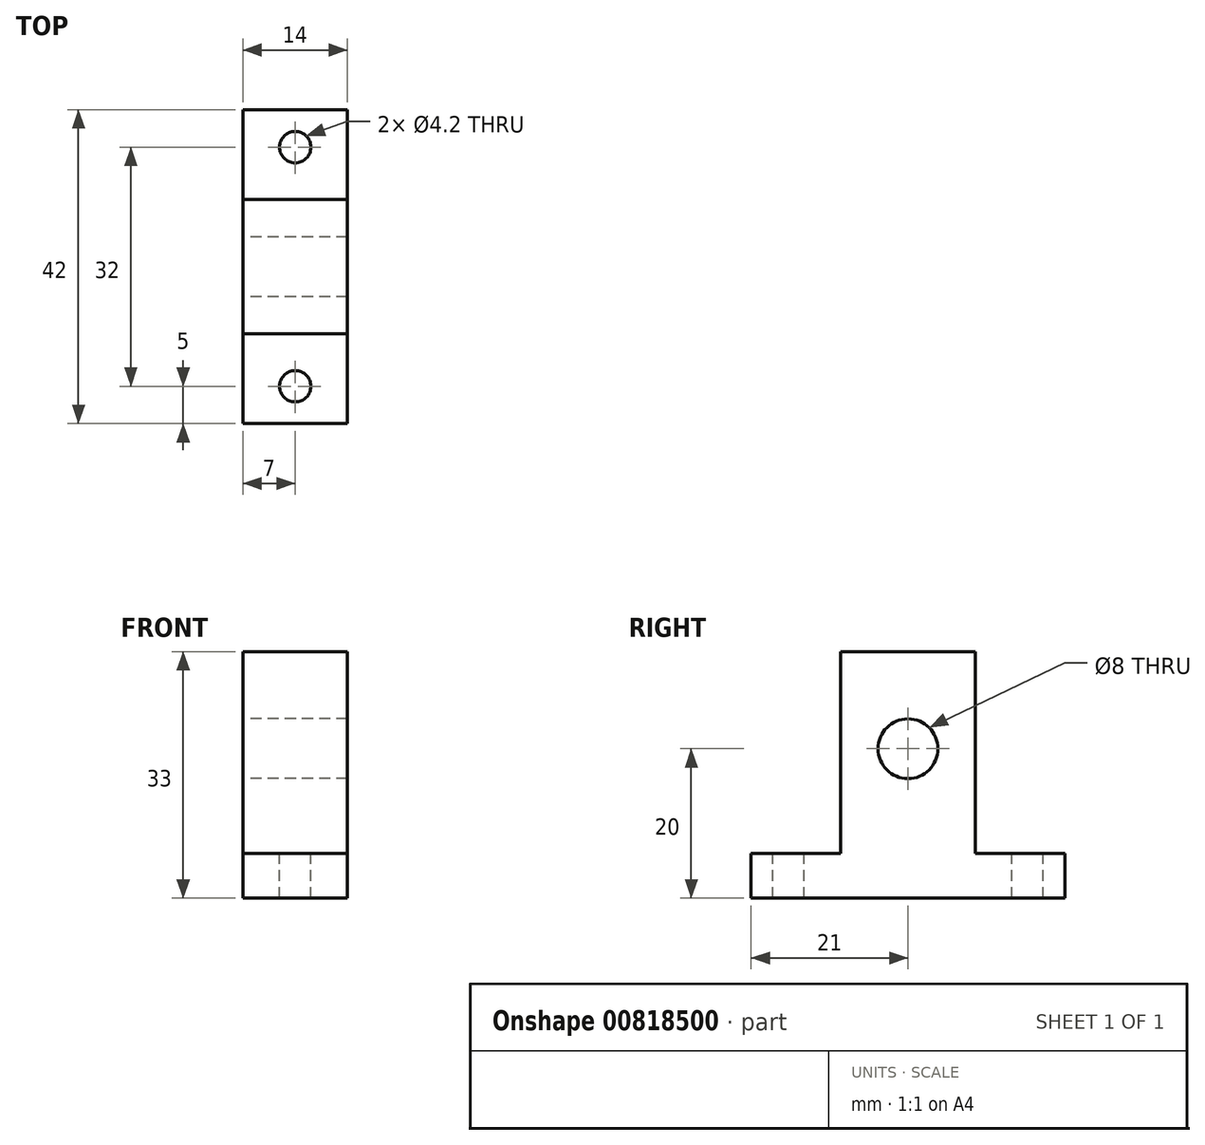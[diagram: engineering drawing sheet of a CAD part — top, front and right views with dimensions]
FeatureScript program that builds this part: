
annotation { "Feature Type Name" : "Feature", "Feature Type Description" : "" }
export const myFeature = defineFeature(function(context is Context, id is Id, definition is map)
    precondition{}
    {
        {
            var Q0;
            Q0=qCreatedBy(makeId("Right.planeOp"),FACE);
            var sketch = newSketch(context, id + "F0", { "sketchPlane" : qUnion([Q0])});
            skCircle(sketch, "E0", {"center": v(0, 20) * mm, "radius": 4 * mm});
            skLineSegment(sketch, "E1", {"start": v(0, 0) * mm, "end": v(-21, 0) * mm});
            skLineSegment(sketch, "E2", {"start": v(-21, 0) * mm, "end": v(-21, 6) * mm});
            skLineSegment(sketch, "E3", {"start": v(-21, 6) * mm, "end": v(-9, 6) * mm});
            skLineSegment(sketch, "E4", {"start": v(-9, 6) * mm, "end": v(-9, 33) * mm});
            skLineSegment(sketch, "E5", {"start": v(-9, 33) * mm, "end": v(0, 33) * mm});
            skLineSegment(sketch, "E6.MirrorCS", {"start": v(0, 0) * mm, "end": v(21, 0) * mm});
            skLineSegment(sketch, "E7.MirrorCS", {"start": v(21, 0) * mm, "end": v(21, 6) * mm});
            skLineSegment(sketch, "E8.MirrorCS", {"start": v(21, 6) * mm, "end": v(9, 6) * mm});
            skLineSegment(sketch, "E9.MirrorCS", {"start": v(9, 33) * mm, "end": v(0, 33) * mm});
            skLineSegment(sketch, "E10.MirrorCS", {"start": v(9, 6) * mm, "end": v(9, 33) * mm});
            skSolve(sketch);
        }
        {
            var Q0;
            Q0=makeQuery(id+"F0.imprint","IMPRINT",FACE,{"disambiguationData":[TD([[makeQuery(id+"F0.imprint","IMPRINT",EDGE,{"derivedFrom":sQuery(id+"F0.wireOp",EDGE,"E0")}),-1.0]])]});
            extrude(context, id + "F1", {"entities" : qUnion([Q0]), "endBound" : BoundingType.SYMMETRIC, "depth" : 14 * mm});
        }
        {
            var Q0;
            Q0=makeQuery(id+"F1.opExtrude","SWEPT_FACE",FACE,{"disambiguationData":[OSD([sQuery(id+"F0.wireOp",EDGE,"E3")])]});
            var sketch = newSketch(context, id + "F2", { "sketchPlane" : qUnion([Q0])});
            skSolve(sketch);
        }
        {
            var Q0;
            {var subQ0=sQuery(id+"F0.wireOp",EDGE,"E3");Q0=makeQuery(id+"F2.imprint","IMPRINT",FACE,{"disambiguationData":[TD([[makeQuery(id+"F2.imprint","IMPRINT",EDGE,{"derivedFrom":makeQuery(id+"F1.opExtrude","CAP_EDGE",EDGE,{"disambiguationData":[OSD([subQ0])],"isStart":true})}),-1.0]])]});}
            var sketch = newSketch(context, id + "F3", { "sketchPlane" : qUnion([Q0])});
            skPoint(sketch, "E11", {"position": v(0, -16) * mm});
            skPoint(sketch, "E12.MirrorP", {"position": v(0, 16) * mm});
            skSolve(sketch);
        }
        {
            var Q0;
            Q0=sQuery(id+"F3.wireOp",VERTEX,"E11");
            var Q1;
            Q1=sQuery(id+"F3.wireOp",VERTEX,"E12.MirrorP");
            var Q2;
            Q2=makeQuery(id+"F1.opExtrude","SWEPT_BODY",BODY,{"disambiguationData":[OSD([sQuery(id+"F0.wireOp",EDGE,"E0"),sQuery(id+"F0.wireOp",EDGE,"E1"),sQuery(id+"F0.wireOp",EDGE,"E2"),sQuery(id+"F0.wireOp",EDGE,"E3"),sQuery(id+"F0.wireOp",EDGE,"E4"),sQuery(id+"F0.wireOp",EDGE,"E5"),sQuery(id+"F0.wireOp",EDGE,"E6.MirrorCS"),sQuery(id+"F0.wireOp",EDGE,"E7.MirrorCS"),sQuery(id+"F0.wireOp",EDGE,"E8.MirrorCS"),sQuery(id+"F0.wireOp",EDGE,"E9.MirrorCS"),sQuery(id+"F0.wireOp",EDGE,"E10.MirrorCS")])]});
            hole(context, id + "F4", {"style" : HoleStyle.SIMPLE, "endStyle" : HoleEndStyle.THROUGH, "holeDiameter" : 4.2 * mm, "tappedDepth" : 12 * mm, "tapClearance" : 3, "locations" : qUnion([Q0, Q1]), "scope" : qUnion([Q2])});
        }
    });
